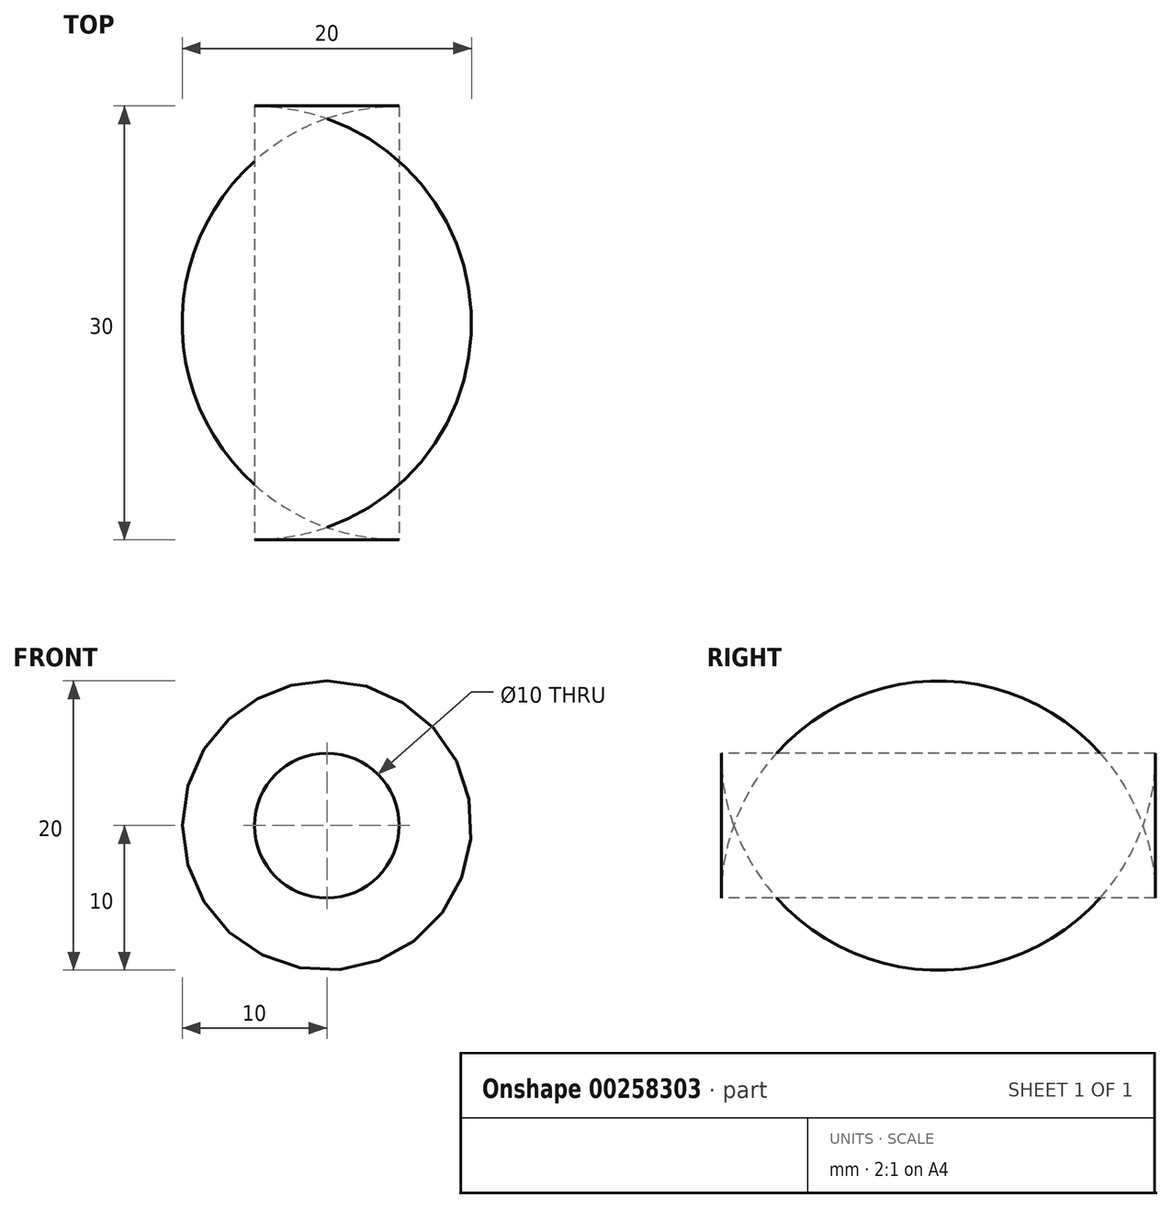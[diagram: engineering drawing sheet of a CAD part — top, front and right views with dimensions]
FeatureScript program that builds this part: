
annotation { "Feature Type Name" : "Feature", "Feature Type Description" : "" }
export const myFeature = defineFeature(function(context is Context, id is Id, definition is map)
    precondition{}
    {
        {
            var Q0;
            Q0=qCreatedBy(makeId("Right.planeOp"),FACE);
            var sketch = newSketch(context, id + "F0", { "sketchPlane" : qUnion([Q0])});
            skLineSegment(sketch, "E0.bottom", {"start": v(-15, -5) * mm, "end": v(15, -5) * mm});
            skLineSegment(sketch, "E0.top", {"start": v(-15, 5) * mm, "end": v(15, 5) * mm});
            skLineSegment(sketch, "E0.left", {"start": v(-15, -5) * mm, "end": v(-15, 5) * mm});
            skLineSegment(sketch, "E0.right", {"start": v(15, -5) * mm, "end": v(15, 5) * mm});
            skPoint(sketch, "E0.middle", {"position": v(0, 0) * mm});
            skArc(sketch, "E1", {"start": v(15, 5) * mm, "mid": v(0, 20) * mm, "end": v(-15, 5) * mm});
            skLineSegment(sketch, "E2", {"start": v(-25.38, 0) * mm, "end": v(35.6, 0) * mm, "construction": true});
            skSolve(sketch);
        }
        {
            var Q0;
            Q0=makeQuery(id+"F0.imprint","IMPRINT",FACE,{"disambiguationData":[TD([[makeQuery(id+"F0.imprint","IMPRINT",EDGE,{"derivedFrom":sQuery(id+"F0.wireOp",EDGE,"E0.top")}),1.0]])]});
            var Q1;
            Q1=sQuery(id+"F0.wireOp",EDGE,"E2");
            revolve(context, id + "F1", {"surfaceOperationType" : NewSurfaceOperationType.NEW, "entities" : qUnion([Q0]), "axis" : qUnion([Q1]), "revolveType" : RevolveType.FULL});
        }
    });
